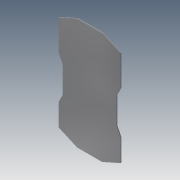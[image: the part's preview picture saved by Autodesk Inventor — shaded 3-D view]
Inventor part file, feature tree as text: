
AUTODESK INVENTOR PART (.ipt)
format: ipt  version: 2013 (Build 170138000, 138)  size: 153,600 bytes
history: native  units: mm
features: sketch x11, extrude x1, hole x1
ambient origin geometry x8: Origin, YZ Plane, XZ Plane, XY Plane, X Axis, Y Axis, Z Axis, Center Point
bodies: Solid1 (feature_tree)
feature tree (13):
  extrude  "Extrusion1"  [1 undecoded]
  sketch  "Sketch2"  dims[d116=0.5mm d117=6.0mm d118=4.0mm d119=2.0mm d120=90.0deg d121=2.0mm d122=0.0mm]
  sketch  "Sketch3"
  sketch  "Sketch4"
  sketch  "Sketch5"
  sketch  "Sketch6"
  sketch  "Sketch7"
  sketch  "Sketch8"
  hole  "Hole1"  [1 undecoded]
  sketch  "Sketch9"
  sketch  "Sketch10"
  sketch  "Sketch11"
  sketch  "Sketch1"  dims[d24=2.0mm d25=0.0mm]
note: 2 required parameter values undecoded (feature->parameter linkage not recoverable at this tier; creation-order binding heuristic only, values carry confidence <= 0.55)
